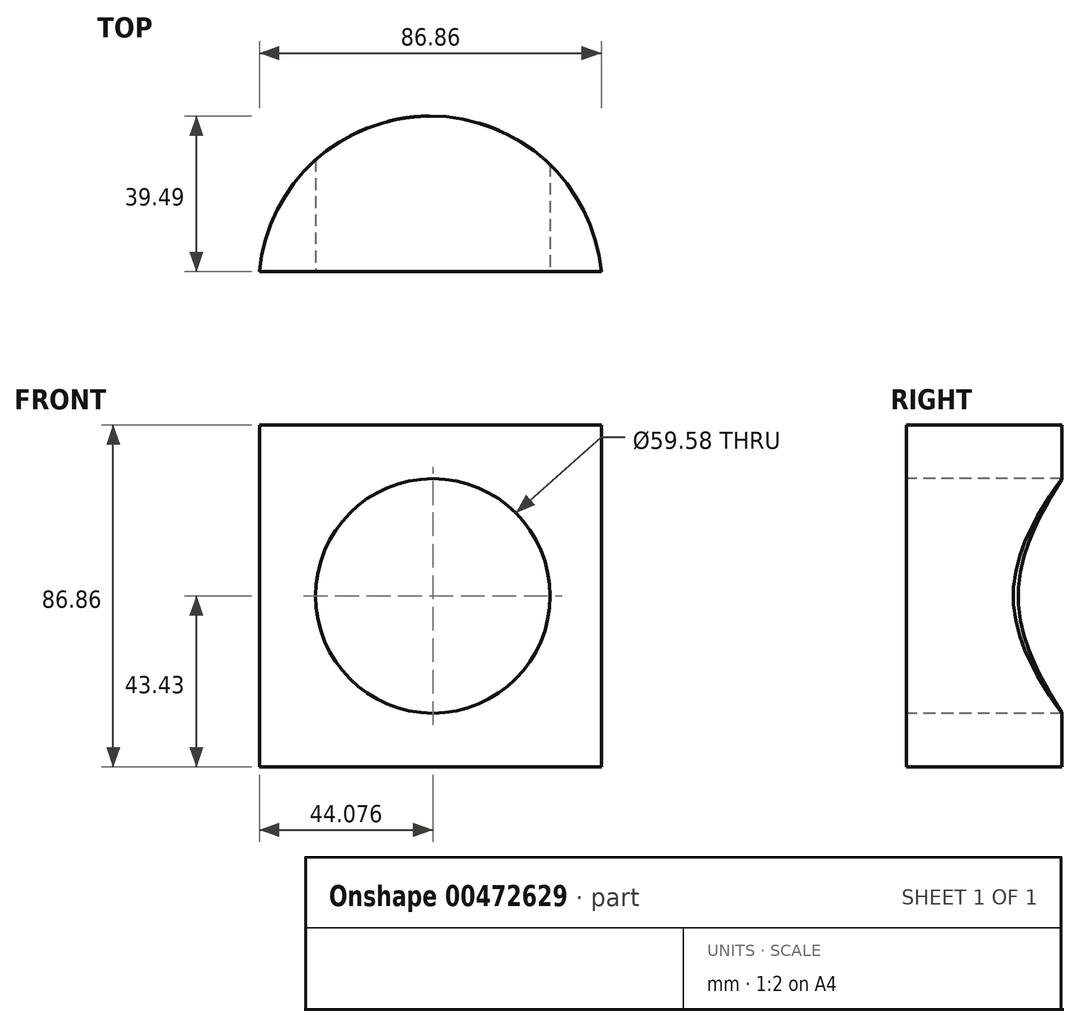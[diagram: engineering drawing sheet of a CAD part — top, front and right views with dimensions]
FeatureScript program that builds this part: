
annotation { "Feature Type Name" : "Feature", "Feature Type Description" : "" }
export const myFeature = defineFeature(function(context is Context, id is Id, definition is map)
    precondition{}
    {
        {
            var Q0;
            Q0=qCreatedBy(makeId("Front.planeOp"),FACE);
            var sketch = newSketch(context, id + "F0", { "sketchPlane" : qUnion([Q0])});
            skLineSegment(sketch, "E0.bottom", {"start": v(-39.46, 43.43) * mm, "end": v(47.4, 43.43) * mm});
            skLineSegment(sketch, "E0.top", {"start": v(-39.46, -43.43) * mm, "end": v(47.4, -43.43) * mm});
            skLineSegment(sketch, "E0.left", {"start": v(-39.46, 43.43) * mm, "end": v(-39.46, -43.43) * mm});
            skLineSegment(sketch, "E0.right", {"start": v(47.4, 43.43) * mm, "end": v(47.4, -43.43) * mm});
            skPoint(sketch, "E0.middle", {"position": v(3.97, 0) * mm});
            skSolve(sketch);
        }
        {
            var Q0;
            Q0 = qSketchRegion(id + "F0", true);
            extrude(context, id + "F1", {"entities" : qUnion([Q0]), "depth" : 86.87 * mm});
        }
        {
            var Q0;
            Q0=makeQuery(id+"F1.opExtrude","SWEPT_FACE",FACE,{"disambiguationData":[OSD([sQuery(id+"F0.wireOp",EDGE,"E0.bottom")])]});
            var sketch = newSketch(context, id + "F2", { "sketchPlane" : qUnion([Q0])});
            skArc(sketch, "E1", {"start": v(47.4, -86.87) * mm, "mid": v(3.97, -47.38) * mm, "end": v(-39.46, -86.87) * mm});
            skSolve(sketch);
        }
        {
            var Q0;
            Q0=makeQuery(id+"F2.imprint","IMPRINT",FACE,{"disambiguationData":[TD([[makeQuery(id+"F2.imprint","IMPRINT",EDGE,{"derivedFrom":sQuery(id+"F2.wireOp",EDGE,"E1")}),-1.0]])]});
            extrude(context, id + "F3", {"entities" : qUnion([Q0]), "operationType" : NewBodyOperationType.REMOVE, "oppositeDirection" : true, "depth" : 86.87 * mm});
        }
        {
            var Q0;
            Q0=makeQuery(id+"F1.opExtrude","CAP_FACE",FACE,{"disambiguationData":[OSD([sQuery(id+"F0.wireOp",EDGE,"E0.bottom"),sQuery(id+"F0.wireOp",EDGE,"E0.top"),sQuery(id+"F0.wireOp",EDGE,"E0.left"),sQuery(id+"F0.wireOp",EDGE,"E0.right")])],"isStart":false});
            var sketch = newSketch(context, id + "F4", { "sketchPlane" : qUnion([Q0])});
            skCircle(sketch, "E2", {"center": v(4.62, 0) * mm, "radius": 29.8 * mm});
            skSolve(sketch);
        }
        {
            var Q0;
            Q0=makeQuery(id+"F4.imprint","IMPRINT",FACE,{"disambiguationData":[TD([[makeQuery(id+"F4.imprint","IMPRINT",EDGE,{"derivedFrom":sQuery(id+"F4.wireOp",EDGE,"E2")}),1.0]])]});
            extrude(context, id + "F5", {"entities" : qUnion([Q0]), "operationType" : NewBodyOperationType.REMOVE, "oppositeDirection" : true, "depth" : 76.2 * mm});
        }
    });
